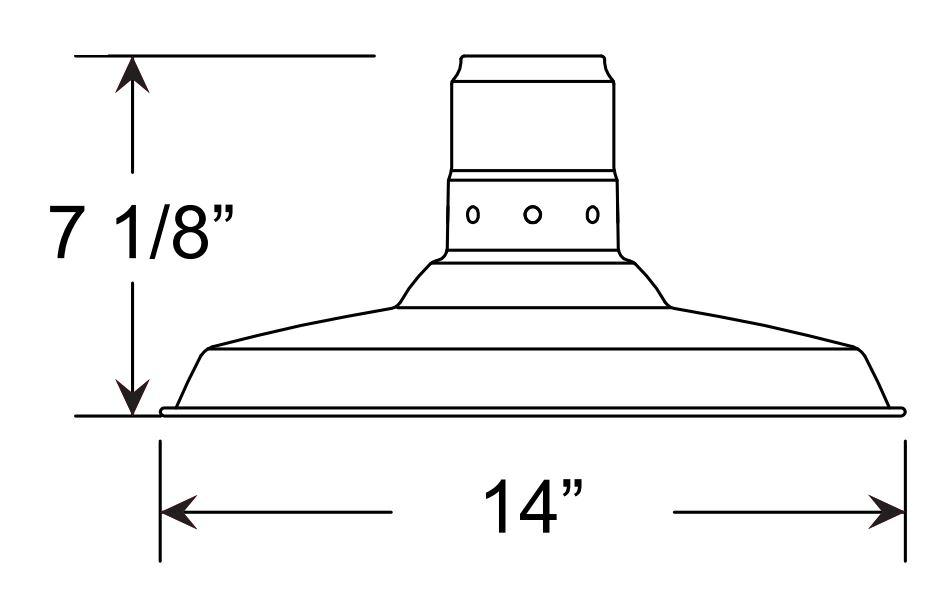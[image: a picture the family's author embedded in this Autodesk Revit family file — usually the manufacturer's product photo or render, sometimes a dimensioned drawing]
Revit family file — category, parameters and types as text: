
# Revit family: Contempo Bistro BBU
name_source: partatom
category: Lighting Fixtures
units: mm (PartAtom-declared; Revit-internal decimal feet)

## family parameters
Always vertical = Yes
Cut with Voids When Loaded = No
Light Source = Yes
OmniClass Number = 23.80.70.00
OmniClass Title = Lighting
Part Type = Normal
Room Calculation Point = No
Round Connector Dimension = Use Diameter
Shared = No
Work Plane-Based = No

## types (4) — shared parameters
BULB = Yes
Body Colour = Spun aluminium
Body Material = body
CRI = >90
Canopy Body = Aqua Green
Color Filter = 16777215
Construction Material = Heavy Duty spun aluminum.
Default Elevation = 0' - 0"
Description = 120-277 Voltage
Dimming = 1%
Dimming Lamp Color Temperature Shift = <None>
Efficiency = 65-125 lumens per watt
HUB = Putty
Life = L70 50,000 hours
Load Classification = Lighting
Manufacturer = ANP Lighting
Photometric Web File = generic
Power Factor = 1
Tilt Angle = 90.00°
URL = https://www.anplighting.com
Voltage = 120 V
Warranty = 5 year limited warranty
b = 0' - 3"

## per-type parameters (varying)
| type | Apparent Load | BBU14 | BBU16 | BBU19 | BBU22 | Fixture Diameter | Fixture Height | Wattage Comments | Weight | a |
| BBU14 | 200 VA | Yes | No | No | No | 1' - 2" | 0' - 8 1/2" | 200W | 3.7lb | 0' - 10" |
| BBU16 | 10 VA | No | Yes | No | No | 1' - 4" | 0' - 9" | 200W | 4.2lb | 0' - 9" |
| BBU19 | 200 VA | No | No | Yes | No | 1' - 7" | 0' - 10 1/4" | 200 W | 5.7 lb | 0' - 11" |
| BBU22 | 200 VA | No | No | No | Yes | 1' - 10" | 0' - 11" | 200 W | 6.2 lb | 0' - 11" |

note: column(s) folded — value = type name in every type: Model

## geometry (parser evidence)
native form markers: Sweep x37
no freeform markers — native parametric forms only
